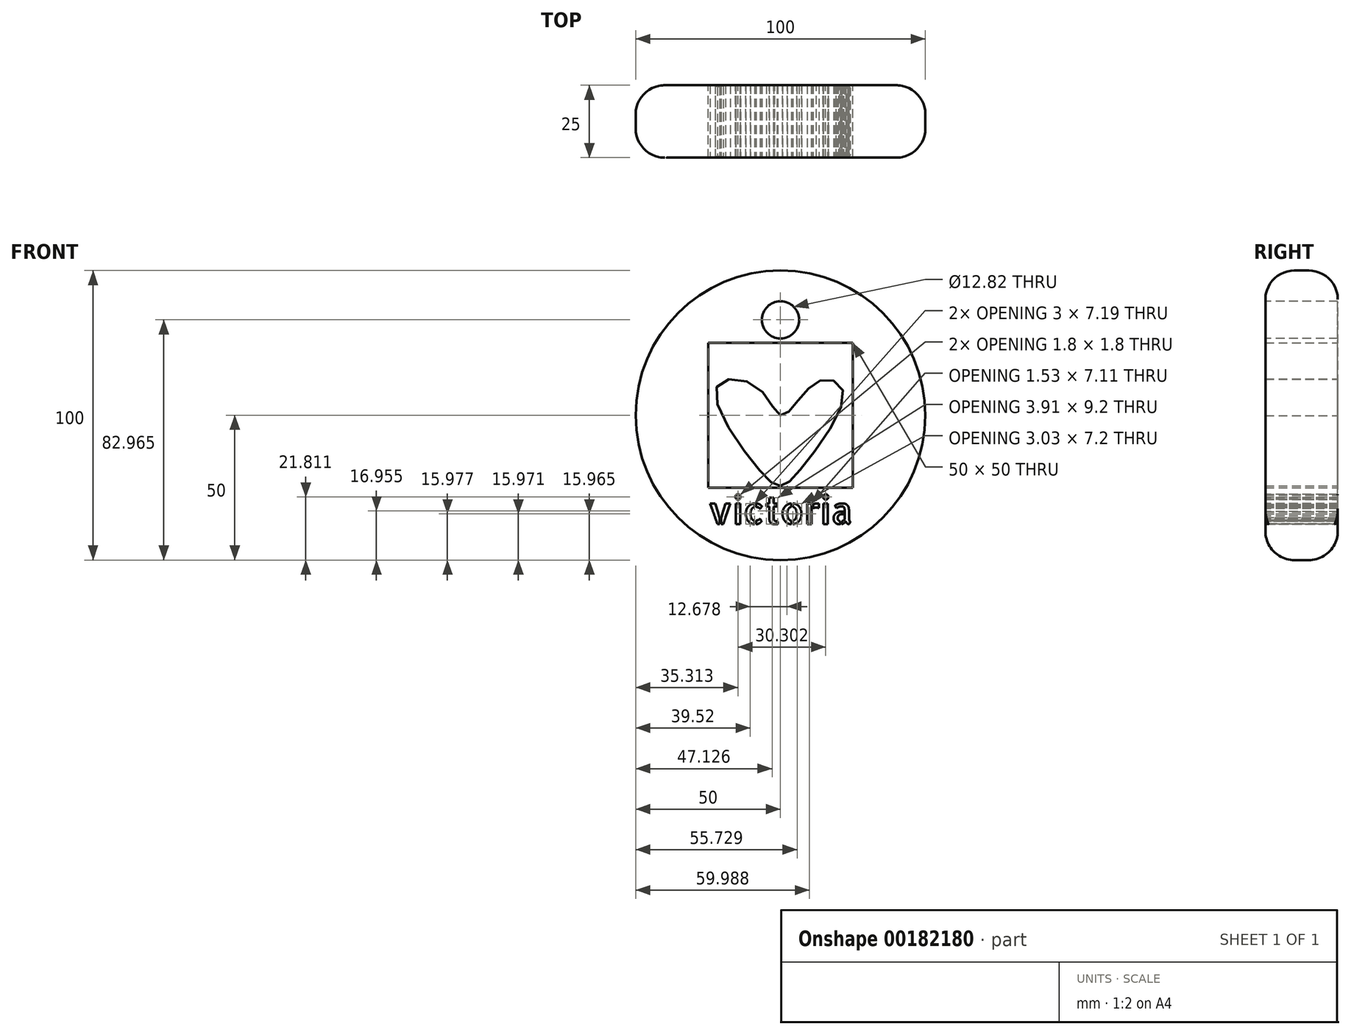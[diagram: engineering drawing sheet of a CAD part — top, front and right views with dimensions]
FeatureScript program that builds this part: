
annotation { "Feature Type Name" : "Feature", "Feature Type Description" : "" }
export const myFeature = defineFeature(function(context is Context, id is Id, definition is map)
    precondition{}
    {
        {
            var Q0;
            Q0=qCreatedBy(makeId("Front.planeOp"),FACE);
            var sketch = newSketch(context, id + "F0", { "sketchPlane" : qUnion([Q0])});
            skCircle(sketch, "E0", {"center": v(0, 0) * mm, "radius": 50 * mm});
            skSolve(sketch);
        }
        {
            var Q0;
            Q0 = qSketchRegion(id + "F0", true);
            extrude(context, id + "F1", {"entities" : qUnion([Q0]), "depth" : 25 * mm});
        }
        {
            var Q0;
            Q0=qCreatedBy(makeId("Front.planeOp"),FACE);
            var sketch = newSketch(context, id + "F2", { "sketchPlane" : qUnion([Q0])});
            skLineSegment(sketch, "E1.bottom", {"start": v(25, -25) * mm, "end": v(-25, -25) * mm});
            skLineSegment(sketch, "E1.top", {"start": v(25, 25) * mm, "end": v(-25, 25) * mm});
            skLineSegment(sketch, "E1.left", {"start": v(25, -25) * mm, "end": v(25, 25) * mm});
            skLineSegment(sketch, "E1.right", {"start": v(-25, -25) * mm, "end": v(-25, 25) * mm});
            skPoint(sketch, "E1.middle", {"position": v(0, 0) * mm});
            skSolve(sketch);
        }
        {
            var Q0;
            Q0 = qSketchRegion(id + "F2", true);
            extrude(context, id + "F3", {"entities" : qUnion([Q0]), "operationType" : NewBodyOperationType.REMOVE, "depth" : 26 * mm});
        }
        {
            var Q0;
            Q0=makeQuery(id+"F1.opExtrude","CAP_FACE",FACE,{"disambiguationData":[OSD([sQuery(id+"F0.wireOp",EDGE,"E0")])],"isStart":false});
            var sketch = newSketch(context, id + "F4", { "sketchPlane" : qUnion([Q0])});
            skText(sketch, "E2", { "text": "victoria", "fontName": "AllertaStencil-Regular.ttf"});
            const initialGuessF4  = {"E2": [-0.025, -0.03758, 1, 0, 0.0093]};
            skSetInitialGuess(sketch, initialGuessF4);
            skSolve(sketch);
        }
        {
            var Q0;
            Q0 = qSketchRegion(id + "F4", true);
            extrude(context, id + "F5", {"entities" : qUnion([Q0]), "operationType" : NewBodyOperationType.REMOVE, "oppositeDirection" : true, "depth" : 26 * mm});
        }
        {
            var Q0;
            Q0=makeQuery(id+"F1.opExtrude","CAP_EDGE",EDGE,{"disambiguationData":[OSD([sQuery(id+"F0.wireOp",EDGE,"E0")])],"isStart":false});
            fillet(context, id + "F6", {"entities" : qUnion([Q0]), "radius" : 10 * mm, "tangentPropagation" : true, "allowEdgeOverflow" : false});
        }
        {
            var Q0;
            Q0=makeQuery(id+"F1.opExtrude","CAP_EDGE",EDGE,{"disambiguationData":[OSD([sQuery(id+"F0.wireOp",EDGE,"E0")])],"isStart":true});
            fillet(context, id + "F7", {"entities" : qUnion([Q0]), "radius" : 10 * mm, "tangentPropagation" : true, "allowEdgeOverflow" : false});
        }
        {
            var Q0;
            Q0=makeQuery(id+"F6.opFillet","SPLIT",FACE,{"disambiguationData":[OD(1.0)],"derivedFrom":makeQuery(id+"F1.opExtrude","CAP_FACE",FACE,{"disambiguationData":[OSD([sQuery(id+"F0.wireOp",EDGE,"E0")])],"isStart":false})});
            var sketch = newSketch(context, id + "F8", { "sketchPlane" : qUnion([Q0])});
            skCircle(sketch, "E3", {"center": v(0, 32.97) * mm, "radius": 6.41 * mm});
            skSolve(sketch);
        }
        {
            var Q0;
            Q0=makeQuery(id+"F8.imprint","IMPRINT",FACE,{"disambiguationData":[TD([[makeQuery(id+"F8.imprint","IMPRINT",EDGE,{"derivedFrom":sQuery(id+"F8.wireOp",EDGE,"E3")}),1.0]])]});
            extrude(context, id + "F9", {"entities" : qUnion([Q0]), "operationType" : NewBodyOperationType.REMOVE, "oppositeDirection" : true, "depth" : 26 * mm});
        }
        {
            var Q0;
            Q0=qCreatedBy(makeId("Front.planeOp"),FACE);
            var sketch = newSketch(context, id + "F10", { "sketchPlane" : qUnion([Q0])});
            skFitSpline(sketch, "E4", {"points": [v(0, 0) * mm, v(-8.53, 10.13) * mm, v(-22.04, 9.77) * mm, v(-8.17, -17.95) * mm, v(0, -24.35) * mm, v(7.46, -17.95) * mm, v(21.68, 8) * mm, v(14.57, 12.26) * mm, v(5.33, 4.09) * mm, v(0, 0) * mm]});
            skSolve(sketch);
        }
        {
            var Q0;
            Q0=makeQuery(id+"F10.imprint","IMPRINT",FACE,{"disambiguationData":[TD([[makeQuery(id+"F10.imprint","IMPRINT",EDGE,{"derivedFrom":sQuery(id+"F10.wireOp",EDGE,"E4")}),1.0]])]});
            extrude(context, id + "F11", {"entities" : qUnion([Q0]), "depth" : 25 * mm});
        }
    });
